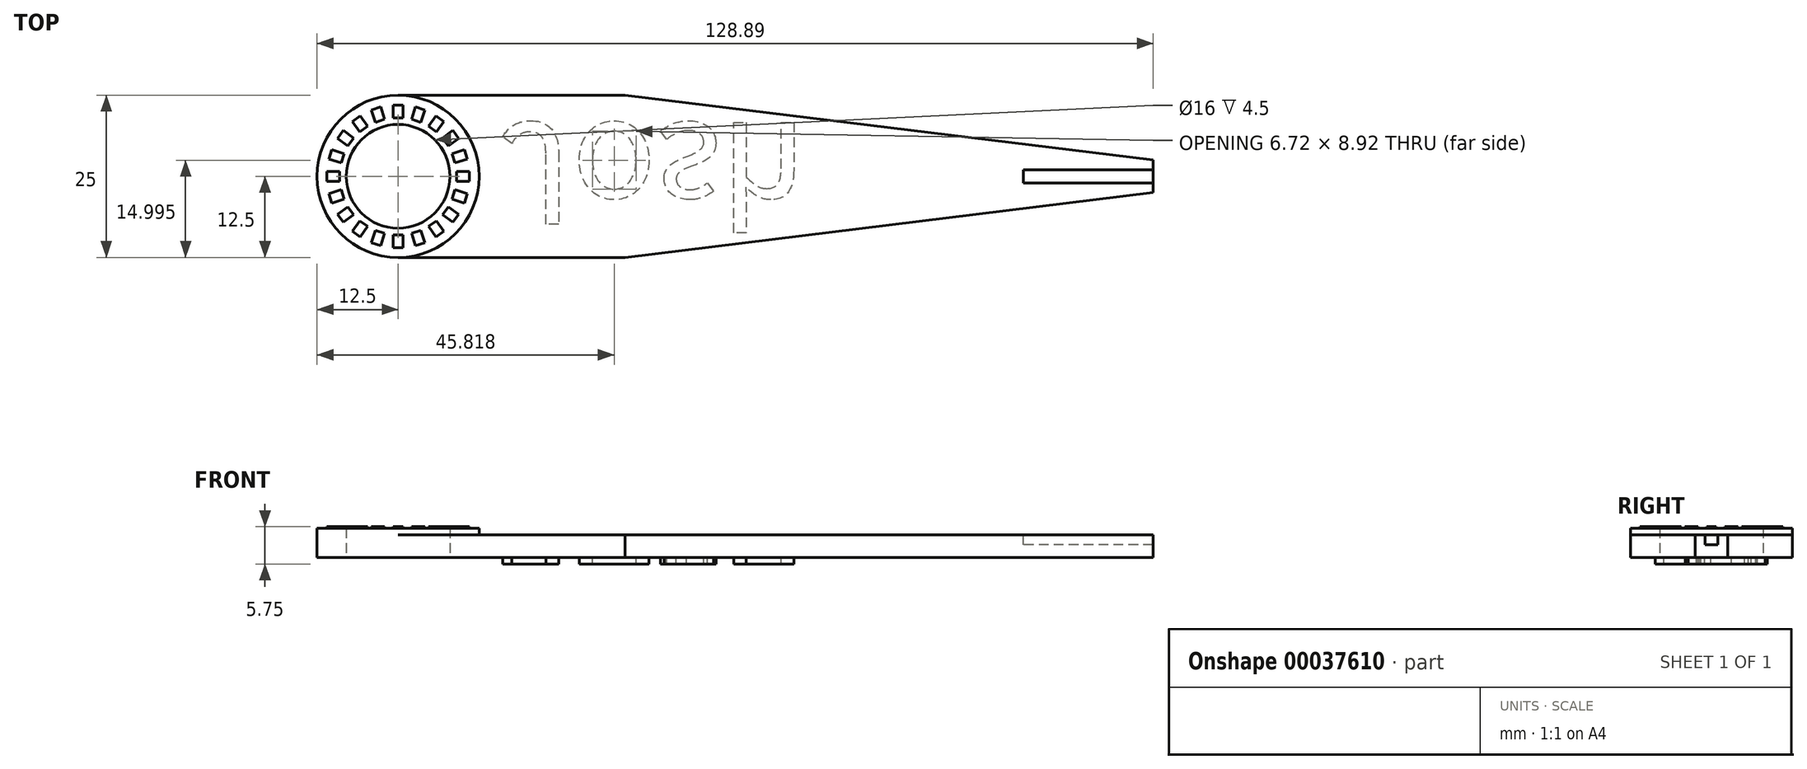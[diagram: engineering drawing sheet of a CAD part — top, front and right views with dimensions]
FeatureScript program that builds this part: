
annotation { "Feature Type Name" : "Feature", "Feature Type Description" : "" }
export const myFeature = defineFeature(function(context is Context, id is Id, definition is map)
    precondition{}
    {
        {
            var Q0;
            Q0=qCreatedBy(makeId("Top.planeOp"),FACE);
            var sketch = newSketch(context, id + "F0", { "sketchPlane" : qUnion([Q0])});
            skCircle(sketch, "E0", {"center": v(0, 0) * mm, "radius": 8 * mm});
            skCircle(sketch, "E1", {"center": v(0, 0) * mm, "radius": 12.5 * mm});
            skLineSegment(sketch, "E2", {"start": v(0, 12.5) * mm, "end": v(35, 12.5) * mm});
            skPoint(sketch, "E3", {"position": v(0, 12.5) * mm});
            skLineSegment(sketch, "E4", {"start": v(0, 0) * mm, "end": v(34.4, 0) * mm, "construction": true});
            skLineSegment(sketch, "E5.MirrorCS", {"start": v(0, -12.5) * mm, "end": v(35, -12.5) * mm});
            skLineSegment(sketch, "E6", {"start": v(35, 12.5) * mm, "end": v(100, 12.5) * mm, "construction": true});
            skLineSegment(sketch, "E7", {"start": v(35, 12.5) * mm, "end": v(116.39, 2.5) * mm});
            skLineSegment(sketch, "E8.MirrorCS", {"start": v(35, -12.5) * mm, "end": v(116.39, -2.5) * mm});
            skLineSegment(sketch, "E9", {"start": v(116.39, -2.5) * mm, "end": v(116.39, 2.5) * mm});
            skSolve(sketch);
        }
        {
            var Q0;
            Q0 = qSketchRegion(id + "F0", true);
            extrude(context, id + "F1", {"entities" : qUnion([Q0]), "depth" : 3.5 * mm});
        }
        {
            var Q0;
            Q0=makeQuery(id+"F1.opExtrude","CAP_FACE",FACE,{"disambiguationData":[OSD([sQuery(id+"F0.wireOp",EDGE,"E0"),sQuery(id+"F0.wireOp",EDGE,"E1"),sQuery(id+"F0.wireOp",EDGE,"E2"),sQuery(id+"F0.wireOp",EDGE,"E5.MirrorCS"),sQuery(id+"F0.wireOp",EDGE,"E7"),sQuery(id+"F0.wireOp",EDGE,"E8.MirrorCS"),sQuery(id+"F0.wireOp",EDGE,"E9")])],"isStart":false});
            var sketch = newSketch(context, id + "F2", { "sketchPlane" : qUnion([Q0])});
            skCircle(sketch, "E10", {"center": v(0, 0) * mm, "radius": 12.5 * mm});
            skCircle(sketch, "E11", {"center": v(0, 0) * mm, "radius": 8 * mm});
            skSolve(sketch);
        }
        {
            var Q0;
            Q0 = qSketchRegion(id + "F2", true);
            var Q1;
            Q1 = qSketchRegion(id + "F4", true);
            extrude(context, id + "F3", {"entities" : qUnion([Q0, Q1]), "operationType" : NewBodyOperationType.ADD, "depth" : 1 * mm});
        }
        {
            var Q0;
            Q0=makeQuery(id+"F3.opExtrude","CAP_FACE",FACE,{"disambiguationData":[OSD([sQuery(id+"F2.wireOp",EDGE,"E10"),sQuery(id+"F2.wireOp",EDGE,"E11")])],"isStart":false});
            var sketch = newSketch(context, id + "F4", { "sketchPlane" : qUnion([Q0])});
            skLineSegment(sketch, "E12.bottom", {"start": v(-0.75, 11) * mm, "end": v(0.75, 11) * mm});
            skLineSegment(sketch, "E12.top", {"start": v(-0.75, 9) * mm, "end": v(0.75, 9) * mm});
            skLineSegment(sketch, "E12.left", {"start": v(-0.75, 11) * mm, "end": v(-0.75, 9) * mm});
            skLineSegment(sketch, "E12.right", {"start": v(0.75, 11) * mm, "end": v(0.75, 9) * mm});
            skPoint(sketch, "E13", {"position": v(0, 8) * mm});
            skLineSegment(sketch, "E14.1.0", {"start": v(-4.11, 10.23) * mm, "end": v(-2.69, 10.7) * mm});
            skLineSegment(sketch, "E14.1.1", {"start": v(-2.69, 10.7) * mm, "end": v(-2.07, 8.8) * mm});
            skLineSegment(sketch, "E14.1.2", {"start": v(-4.11, 10.23) * mm, "end": v(-3.5, 8.33) * mm});
            skLineSegment(sketch, "E14.1.3", {"start": v(-3.5, 8.33) * mm, "end": v(-2.07, 8.8) * mm});
            skLineSegment(sketch, "E14.2.0", {"start": v(-7.07, 8.46) * mm, "end": v(-5.86, 9.34) * mm});
            skLineSegment(sketch, "E14.2.1", {"start": v(-5.86, 9.34) * mm, "end": v(-4.68, 7.72) * mm});
            skLineSegment(sketch, "E14.2.2", {"start": v(-7.07, 8.46) * mm, "end": v(-5.9, 6.84) * mm});
            skLineSegment(sketch, "E14.2.3", {"start": v(-5.9, 6.84) * mm, "end": v(-4.68, 7.72) * mm});
            skLineSegment(sketch, "E14.3.0", {"start": v(-9.34, 5.86) * mm, "end": v(-8.46, 7.07) * mm});
            skLineSegment(sketch, "E14.3.1", {"start": v(-8.46, 7.07) * mm, "end": v(-6.84, 5.9) * mm});
            skLineSegment(sketch, "E14.3.2", {"start": v(-9.34, 5.86) * mm, "end": v(-7.72, 4.68) * mm});
            skLineSegment(sketch, "E14.3.3", {"start": v(-7.72, 4.68) * mm, "end": v(-6.84, 5.9) * mm});
            skLineSegment(sketch, "E14.4.0", {"start": v(-10.7, 2.69) * mm, "end": v(-10.23, 4.11) * mm});
            skLineSegment(sketch, "E14.4.1", {"start": v(-10.23, 4.11) * mm, "end": v(-8.33, 3.5) * mm});
            skLineSegment(sketch, "E14.4.2", {"start": v(-10.7, 2.69) * mm, "end": v(-8.8, 2.07) * mm});
            skLineSegment(sketch, "E14.4.3", {"start": v(-8.8, 2.07) * mm, "end": v(-8.33, 3.5) * mm});
            skLineSegment(sketch, "E14.5.0", {"start": v(-11, -0.75) * mm, "end": v(-11, 0.75) * mm});
            skLineSegment(sketch, "E14.5.1", {"start": v(-11, 0.75) * mm, "end": v(-9, 0.75) * mm});
            skLineSegment(sketch, "E14.5.2", {"start": v(-11, -0.75) * mm, "end": v(-9, -0.75) * mm});
            skLineSegment(sketch, "E14.5.3", {"start": v(-9, -0.75) * mm, "end": v(-9, 0.75) * mm});
            skLineSegment(sketch, "E14.6.0", {"start": v(-10.23, -4.11) * mm, "end": v(-10.7, -2.69) * mm});
            skLineSegment(sketch, "E14.6.1", {"start": v(-10.7, -2.69) * mm, "end": v(-8.8, -2.07) * mm});
            skLineSegment(sketch, "E14.6.2", {"start": v(-10.23, -4.11) * mm, "end": v(-8.33, -3.5) * mm});
            skLineSegment(sketch, "E14.6.3", {"start": v(-8.33, -3.5) * mm, "end": v(-8.8, -2.07) * mm});
            skLineSegment(sketch, "E14.7.0", {"start": v(-8.46, -7.07) * mm, "end": v(-9.34, -5.86) * mm});
            skLineSegment(sketch, "E14.7.1", {"start": v(-9.34, -5.86) * mm, "end": v(-7.72, -4.68) * mm});
            skLineSegment(sketch, "E14.7.2", {"start": v(-8.46, -7.07) * mm, "end": v(-6.84, -5.9) * mm});
            skLineSegment(sketch, "E14.7.3", {"start": v(-6.84, -5.9) * mm, "end": v(-7.72, -4.68) * mm});
            skLineSegment(sketch, "E14.8.0", {"start": v(-5.86, -9.34) * mm, "end": v(-7.07, -8.46) * mm});
            skLineSegment(sketch, "E14.8.1", {"start": v(-7.07, -8.46) * mm, "end": v(-5.9, -6.84) * mm});
            skLineSegment(sketch, "E14.8.2", {"start": v(-5.86, -9.34) * mm, "end": v(-4.68, -7.72) * mm});
            skLineSegment(sketch, "E14.8.3", {"start": v(-4.68, -7.72) * mm, "end": v(-5.9, -6.84) * mm});
            skLineSegment(sketch, "E14.9.0", {"start": v(-2.69, -10.7) * mm, "end": v(-4.11, -10.23) * mm});
            skLineSegment(sketch, "E14.9.1", {"start": v(-4.11, -10.23) * mm, "end": v(-3.5, -8.33) * mm});
            skLineSegment(sketch, "E14.9.2", {"start": v(-2.69, -10.7) * mm, "end": v(-2.07, -8.8) * mm});
            skLineSegment(sketch, "E14.9.3", {"start": v(-2.07, -8.8) * mm, "end": v(-3.5, -8.33) * mm});
            skLineSegment(sketch, "E14.10.0", {"start": v(0.75, -11) * mm, "end": v(-0.75, -11) * mm});
            skLineSegment(sketch, "E14.10.1", {"start": v(-0.75, -11) * mm, "end": v(-0.75, -9) * mm});
            skLineSegment(sketch, "E14.10.2", {"start": v(0.75, -11) * mm, "end": v(0.75, -9) * mm});
            skLineSegment(sketch, "E14.10.3", {"start": v(0.75, -9) * mm, "end": v(-0.75, -9) * mm});
            skLineSegment(sketch, "E14.11.0", {"start": v(4.11, -10.23) * mm, "end": v(2.69, -10.7) * mm});
            skLineSegment(sketch, "E14.11.1", {"start": v(2.69, -10.7) * mm, "end": v(2.07, -8.8) * mm});
            skLineSegment(sketch, "E14.11.2", {"start": v(4.11, -10.23) * mm, "end": v(3.5, -8.33) * mm});
            skLineSegment(sketch, "E14.11.3", {"start": v(3.5, -8.33) * mm, "end": v(2.07, -8.8) * mm});
            skLineSegment(sketch, "E14.12.0", {"start": v(7.07, -8.46) * mm, "end": v(5.86, -9.34) * mm});
            skLineSegment(sketch, "E14.12.1", {"start": v(5.86, -9.34) * mm, "end": v(4.68, -7.72) * mm});
            skLineSegment(sketch, "E14.12.2", {"start": v(7.07, -8.46) * mm, "end": v(5.9, -6.84) * mm});
            skLineSegment(sketch, "E14.12.3", {"start": v(5.9, -6.84) * mm, "end": v(4.68, -7.72) * mm});
            skLineSegment(sketch, "E14.13.0", {"start": v(9.34, -5.86) * mm, "end": v(8.46, -7.07) * mm});
            skLineSegment(sketch, "E14.13.1", {"start": v(8.46, -7.07) * mm, "end": v(6.84, -5.9) * mm});
            skLineSegment(sketch, "E14.13.2", {"start": v(9.34, -5.86) * mm, "end": v(7.72, -4.68) * mm});
            skLineSegment(sketch, "E14.13.3", {"start": v(7.72, -4.68) * mm, "end": v(6.84, -5.9) * mm});
            skLineSegment(sketch, "E14.14.0", {"start": v(10.7, -2.69) * mm, "end": v(10.23, -4.11) * mm});
            skLineSegment(sketch, "E14.14.1", {"start": v(10.23, -4.11) * mm, "end": v(8.33, -3.5) * mm});
            skLineSegment(sketch, "E14.14.2", {"start": v(10.7, -2.69) * mm, "end": v(8.8, -2.07) * mm});
            skLineSegment(sketch, "E14.14.3", {"start": v(8.8, -2.07) * mm, "end": v(8.33, -3.5) * mm});
            skLineSegment(sketch, "E14.15.0", {"start": v(11, 0.75) * mm, "end": v(11, -0.75) * mm});
            skLineSegment(sketch, "E14.15.1", {"start": v(11, -0.75) * mm, "end": v(9, -0.75) * mm});
            skLineSegment(sketch, "E14.15.2", {"start": v(11, 0.75) * mm, "end": v(9, 0.75) * mm});
            skLineSegment(sketch, "E14.15.3", {"start": v(9, 0.75) * mm, "end": v(9, -0.75) * mm});
            skLineSegment(sketch, "E14.16.0", {"start": v(10.23, 4.11) * mm, "end": v(10.7, 2.69) * mm});
            skLineSegment(sketch, "E14.16.1", {"start": v(10.7, 2.69) * mm, "end": v(8.8, 2.07) * mm});
            skLineSegment(sketch, "E14.16.2", {"start": v(10.23, 4.11) * mm, "end": v(8.33, 3.5) * mm});
            skLineSegment(sketch, "E14.16.3", {"start": v(8.33, 3.5) * mm, "end": v(8.8, 2.07) * mm});
            skLineSegment(sketch, "E14.17.0", {"start": v(8.46, 7.07) * mm, "end": v(9.34, 5.86) * mm});
            skLineSegment(sketch, "E14.17.1", {"start": v(9.34, 5.86) * mm, "end": v(7.72, 4.68) * mm});
            skLineSegment(sketch, "E14.17.2", {"start": v(8.46, 7.07) * mm, "end": v(6.84, 5.9) * mm});
            skLineSegment(sketch, "E14.17.3", {"start": v(6.84, 5.9) * mm, "end": v(7.72, 4.68) * mm});
            skLineSegment(sketch, "E14.18.0", {"start": v(5.86, 9.34) * mm, "end": v(7.07, 8.46) * mm});
            skLineSegment(sketch, "E14.18.1", {"start": v(7.07, 8.46) * mm, "end": v(5.9, 6.84) * mm});
            skLineSegment(sketch, "E14.18.2", {"start": v(5.86, 9.34) * mm, "end": v(4.68, 7.72) * mm});
            skLineSegment(sketch, "E14.18.3", {"start": v(4.68, 7.72) * mm, "end": v(5.9, 6.84) * mm});
            skLineSegment(sketch, "E14.19.0", {"start": v(2.69, 10.7) * mm, "end": v(4.11, 10.23) * mm});
            skLineSegment(sketch, "E14.19.1", {"start": v(4.11, 10.23) * mm, "end": v(3.5, 8.33) * mm});
            skLineSegment(sketch, "E14.19.2", {"start": v(2.69, 10.7) * mm, "end": v(2.07, 8.8) * mm});
            skLineSegment(sketch, "E14.19.3", {"start": v(2.07, 8.8) * mm, "end": v(3.5, 8.33) * mm});
            skPoint(sketch, "E14.center", {"position": v(0, 0) * mm});
            skSolve(sketch);
        }
        {
            var Q0;
            Q0 = qSketchRegion(id + "F4", true);
            extrude(context, id + "F5", {"entities" : qUnion([Q0]), "operationType" : NewBodyOperationType.ADD, "depth" : .25 * mm});
        }
        {
            var Q0;
            Q0=makeQuery(id+"F1.opExtrude","CAP_FACE",FACE,{"disambiguationData":[OSD([sQuery(id+"F0.wireOp",EDGE,"E0"),sQuery(id+"F0.wireOp",EDGE,"E1"),sQuery(id+"F0.wireOp",EDGE,"E2"),sQuery(id+"F0.wireOp",EDGE,"E5.MirrorCS"),sQuery(id+"F0.wireOp",EDGE,"E7"),sQuery(id+"F0.wireOp",EDGE,"E8.MirrorCS"),sQuery(id+"F0.wireOp",EDGE,"E9")])],"isStart":false});
            var sketch = newSketch(context, id + "F6", { "sketchPlane" : qUnion([Q0])});
            skLineSegment(sketch, "E15.bottom", {"start": v(116.39, 1) * mm, "end": v(96.39, 1) * mm});
            skLineSegment(sketch, "E15.top", {"start": v(116.39, -1) * mm, "end": v(96.39, -1) * mm});
            skLineSegment(sketch, "E15.left", {"start": v(116.39, 1) * mm, "end": v(116.39, -1) * mm});
            skLineSegment(sketch, "E15.right", {"start": v(96.39, 1) * mm, "end": v(96.39, -1) * mm});
            skSolve(sketch);
        }
        {
            var Q0;
            Q0=makeQuery(id+"F1.opExtrude","CAP_FACE",FACE,{"disambiguationData":[OSD([sQuery(id+"F0.wireOp",EDGE,"E0"),sQuery(id+"F0.wireOp",EDGE,"E1"),sQuery(id+"F0.wireOp",EDGE,"E2"),sQuery(id+"F0.wireOp",EDGE,"E5.MirrorCS"),sQuery(id+"F0.wireOp",EDGE,"E7"),sQuery(id+"F0.wireOp",EDGE,"E8.MirrorCS"),sQuery(id+"F0.wireOp",EDGE,"E9")])],"isStart":true});
            var sketch = newSketch(context, id + "F7", { "sketchPlane" : qUnion([Q0])});
            skText(sketch, "E16", { "text": "Josh", "fontName": "NotoSansCJKkr-Regular.otf"});
            const initialGuessF7  = {"E16": [0.0154, -0.0083, 1, 0, 0.01537]};
            skSetInitialGuess(sketch, initialGuessF7);
            skSolve(sketch);
        }
        {
            var Q0;
            Q0 = qSketchRegion(id + "F7", true);
            extrude(context, id + "F8", {"entities" : qUnion([Q0]), "depth" : 1 * mm});
        }
        {
            var Q0;
            Q0 = qSketchRegion(id + "F6", true);
            extrude(context, id + "F9", {"entities" : qUnion([Q0]), "operationType" : NewBodyOperationType.REMOVE, "oppositeDirection" : true, "depth" : 1.5 * mm});
        }
    });
